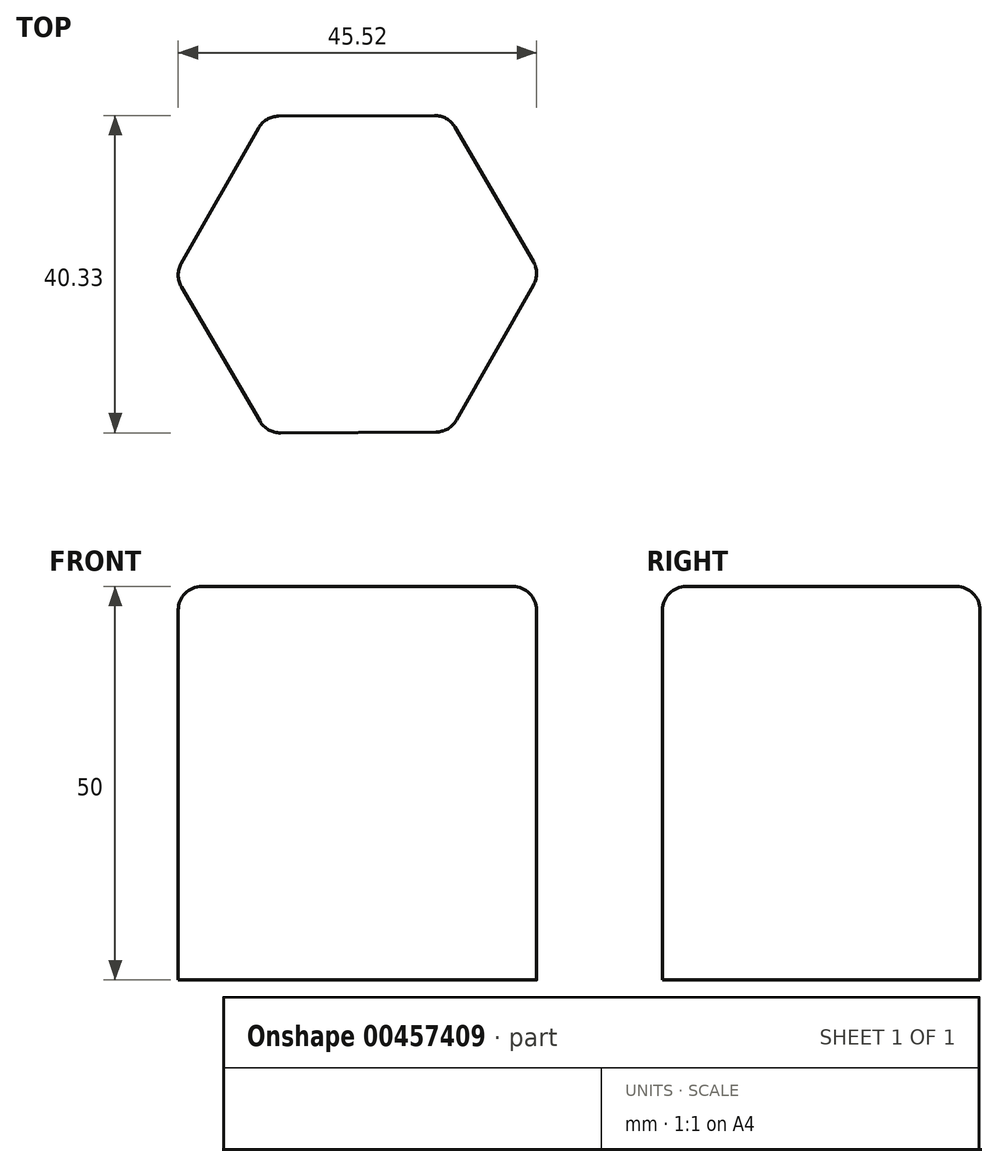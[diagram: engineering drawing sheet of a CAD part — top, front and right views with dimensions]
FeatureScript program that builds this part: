
annotation { "Feature Type Name" : "Feature", "Feature Type Description" : "" }
export const myFeature = defineFeature(function(context is Context, id is Id, definition is map)
    precondition{}
    {
        {
            var Q0;
            Q0=qCreatedBy(makeId("Top.planeOp"),FACE);
            var sketch = newSketch(context, id + "F0", { "sketchPlane" : qUnion([Q0])});
            skCircle(sketch, "E0", {"center": v(-24.17, 11.96) * mm, "radius": 18.14 * mm});
            skPoint(sketch, "E0.first.point", {"position": v(-35.26, 26.31) * mm});
            skPoint(sketch, "E0.second.point", {"position": v(-13.62, -2.8) * mm});
            skPoint(sketch, "E0.third.point", {"position": v(-6.14, 14.03) * mm});
            skCircle(sketch, "E1.cCircle", {"center": v(-38.47, -32.73) * mm, "radius": 20.11 * mm, "construction": true});
            skLineSegment(sketch, "E1.0", {"start": v(-26.97, -12.55) * mm, "end": v(-15.24, -32.6) * mm});
            skLineSegment(sketch, "E1.1", {"start": v(-15.24, -32.6) * mm, "end": v(-26.75, -52.78) * mm});
            skLineSegment(sketch, "E1.2", {"start": v(-26.75, -52.78) * mm, "end": v(-49.97, -52.9) * mm});
            skLineSegment(sketch, "E1.3", {"start": v(-49.97, -52.9) * mm, "end": v(-61.7, -32.85) * mm});
            skLineSegment(sketch, "E1.4", {"start": v(-61.7, -32.85) * mm, "end": v(-50.2, -12.67) * mm});
            skLineSegment(sketch, "E1.5", {"start": v(-50.2, -12.67) * mm, "end": v(-26.97, -12.55) * mm});
            skPoint(sketch, "E1.0.midPoint", {"position": v(-21.1, -22.57) * mm});
            skSolve(sketch);
        }
        {
            var Q0;
            Q0=makeQuery(id+"F0.imprint","IMPRINT",FACE,{"disambiguationData":[TD([[makeQuery(id+"F0.imprint","IMPRINT",EDGE,{"derivedFrom":sQuery(id+"F0.wireOp",EDGE,"E1.0")}),-1.0]])]});
            extrude(context, id + "F1", {"entities" : qUnion([Q0]), "depth" : 50 * mm});
        }
        {
            var Q0;
            Q0=makeQuery(id+"F1.opExtrude","CAP_EDGE",EDGE,{"disambiguationData":[OSD([sQuery(id+"F0.wireOp",EDGE,"E1.5")])],"isStart":false});
            var Q1;
            Q1=makeQuery(id+"F1.opExtrude","CAP_EDGE",EDGE,{"disambiguationData":[OSD([sQuery(id+"F0.wireOp",EDGE,"E1.4")])],"isStart":false});
            var Q2;
            Q2=makeQuery(id+"F1.opExtrude","CAP_EDGE",EDGE,{"disambiguationData":[OSD([sQuery(id+"F0.wireOp",EDGE,"E1.3")])],"isStart":false});
            var Q3;
            Q3=makeQuery(id+"F1.opExtrude","CAP_EDGE",EDGE,{"disambiguationData":[OSD([sQuery(id+"F0.wireOp",EDGE,"E1.0")])],"isStart":false});
            var Q4;
            Q4=makeQuery(id+"F1.opExtrude","CAP_EDGE",EDGE,{"disambiguationData":[OSD([sQuery(id+"F0.wireOp",EDGE,"E1.2")])],"isStart":false});
            var Q5;
            Q5=makeQuery(id+"F1.opExtrude","CAP_EDGE",EDGE,{"disambiguationData":[OSD([sQuery(id+"F0.wireOp",EDGE,"E1.1")])],"isStart":false});
            var Q6;
            Q6=makeQuery(id+"F1.opExtrude","SWEPT_EDGE",EDGE,{"disambiguationData":[OSD([sQuery(id+"F0.wireOp",EDGE,"E1.4"),sQuery(id+"F0.wireOp",EDGE,"E1.5")])]});
            var Q7;
            Q7=makeQuery(id+"F1.opExtrude","SWEPT_EDGE",EDGE,{"disambiguationData":[OSD([sQuery(id+"F0.wireOp",EDGE,"E1.3"),sQuery(id+"F0.wireOp",EDGE,"E1.4")])]});
            var Q8;
            Q8=makeQuery(id+"F1.opExtrude","SWEPT_EDGE",EDGE,{"disambiguationData":[OSD([sQuery(id+"F0.wireOp",EDGE,"E1.0"),sQuery(id+"F0.wireOp",EDGE,"E1.5")])]});
            var Q9;
            Q9=makeQuery(id+"F1.opExtrude","SWEPT_EDGE",EDGE,{"disambiguationData":[OSD([sQuery(id+"F0.wireOp",EDGE,"E1.0"),sQuery(id+"F0.wireOp",EDGE,"E1.1")])]});
            var Q10;
            Q10=makeQuery(id+"F1.opExtrude","SWEPT_EDGE",EDGE,{"disambiguationData":[OSD([sQuery(id+"F0.wireOp",EDGE,"E1.1"),sQuery(id+"F0.wireOp",EDGE,"E1.2")])]});
            var Q11;
            Q11=makeQuery(id+"F1.opExtrude","SWEPT_EDGE",EDGE,{"disambiguationData":[OSD([sQuery(id+"F0.wireOp",EDGE,"E1.2"),sQuery(id+"F0.wireOp",EDGE,"E1.3")])]});
            fillet(context, id + "F2", {"entities" : qUnion([Q0, Q1, Q2, Q3, Q4, Q5, Q6, Q7, Q8, Q9, Q10, Q11]), "radius" : 3 * mm, "tangentPropagation" : true, "allowEdgeOverflow" : false});
        }
    });
